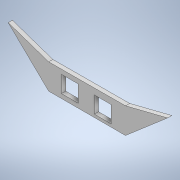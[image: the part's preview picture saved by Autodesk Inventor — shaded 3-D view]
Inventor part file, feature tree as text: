
AUTODESK INVENTOR PART (.ipt)
format: ipt  version: 2020.1 (Build 241239000, 239)  size: 118,784 bytes
history: native  units: in
note: dims shown in document units (in); Inventor stores cm internally (conversion verified against a paired STEP export)
features: extrude x1, sketch x1
ambient origin geometry x8: Origin, YZ Plane, XZ Plane, XY Plane, X Axis, Y Axis, Z Axis, Center Point
bodies: Solid1 (feature_tree)
feature tree (2):
  extrude  "Extrusion1"  Depth=48.0in
  sketch  "Sketch1"  dims[d2=221.0in d5=48.0in d6=48.0in d8=162.0in d11=73.0in d12=123.0in d13=74.0in d14=160.0in d15=125.0in d16=48.0in d17=48.0in d18=12.0in d19=0.0in]
